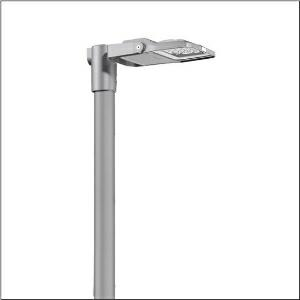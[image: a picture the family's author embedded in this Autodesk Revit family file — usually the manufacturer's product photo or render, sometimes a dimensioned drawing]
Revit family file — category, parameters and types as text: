
# Revit family: floodlight_fl_21_micro___pl61_5xa7762a4c3a_4876
name_source: partatom
category: Lighting Fixtures
units: mm (PartAtom-declared; Revit-internal decimal feet)

## family parameters
Cut with Voids When Loaded = No
Host = Face
Light Source = No
Part Type = Normal
Room Calculation Point = No
Round Connector Dimension = Use Diameter
Shared = No

## types (1)
- --- (1 x LED, 3030 lm, 23.1 W, 4000K)
    Apparent Load = 23 VA
    CIE Flux Codes = 33 65 98 100 100
    Color Rendering = 70
    Color Temperature = 4000K
    Default Elevation = 1800 mm
    Description = Floodlight FL 21 micro, floodlight, primary light control with lens, of PMMA, primary optical cover: protective disc, of toughened safety glass, transparent, light distribution: PL61, light emission: direct distribution, installation type: surface-mounted, LED, High Power LED, rated luminous flux: 3.030lm, luminous efficacy: 131lm/W, light colour: 740, colour temperature: 4000K, control gear: ECG iQ, control: Auto-Match, Temp-Guard, Night-Set, Smart-Wire, Desk-Remote (wireless, voltage-free reading and setting of iQ features in the workshop via application-optimized NFC function/RFID function), optimised constant luminous flux control (CLO 2.0), Street-Remote, with terminal, 6-pole, mains connection: 220..240V, AC, 50/60Hz, start of lifetime: 23W, end of lifetime: 24W, reduction: 11W, luminaire housing, of diecast aluminium, powder-coated, Siteco® metallic grey (DB 702S), corrosivity category C5 according to DIN EN ISO 12944, mast bracket, of steel, galvanised, powder-coated, Siteco® metallic grey (DB 702S), protection rating (complete): IP66, insulation class (complete): insulation class II (safety insulation), certification: CE, protection symbol: D, impact resistance: IK07, permissible operating ambient temperature: -40..+40°C, permissible operating ambient temperature for outdoor applications: -40..+50°C, standard: DIN EN 12944, packaging unit: 1 piece

Light Distribution: PL61
    Height = 65 mm
    Lamp = 1 x LED
    Lamp Light Flux = 3030 lm
    Lamp Power = 23.1 W
    Lamp count = 1
    Length = 312 mm
    Luminous efficacy = 131 lm/W
    Manufacturer = Siteco
    ModVariant = No
    Model = 5XA7762A4C3A
    Number of Poles = 1
    OnlyDefault = Yes
    Power Factor = 1
    Product Name = Floodlight FL 21 micro | PL61
    Product group = floodlight | pylon top
    ProductGroupID = 6101
    Protection Class = Protection class II
    Protection Degree = IP 66
    RLX_Detail_Level = 1
    RlxData = <blob elided: 101753 chars, md5=0e3cfc63>
    Socket = socket
    Standby Power = 0 W
    System Light Flux = 3030 lm
    System Power = 23 W
    Type Comments = factory setting: luminous flux: 100 % | dim-lin: 254 | 455 mA
    Type Image = l_1007121.jpg
    URL = http://relux.com
    VarID = @adj_115183
    Voltage = 0 V
    Weight = 0.00 kg
    Width = 230 mm

## geometry (parser evidence)
native form markers: Blend x4, Sweep x13
no freeform markers — native parametric forms only
